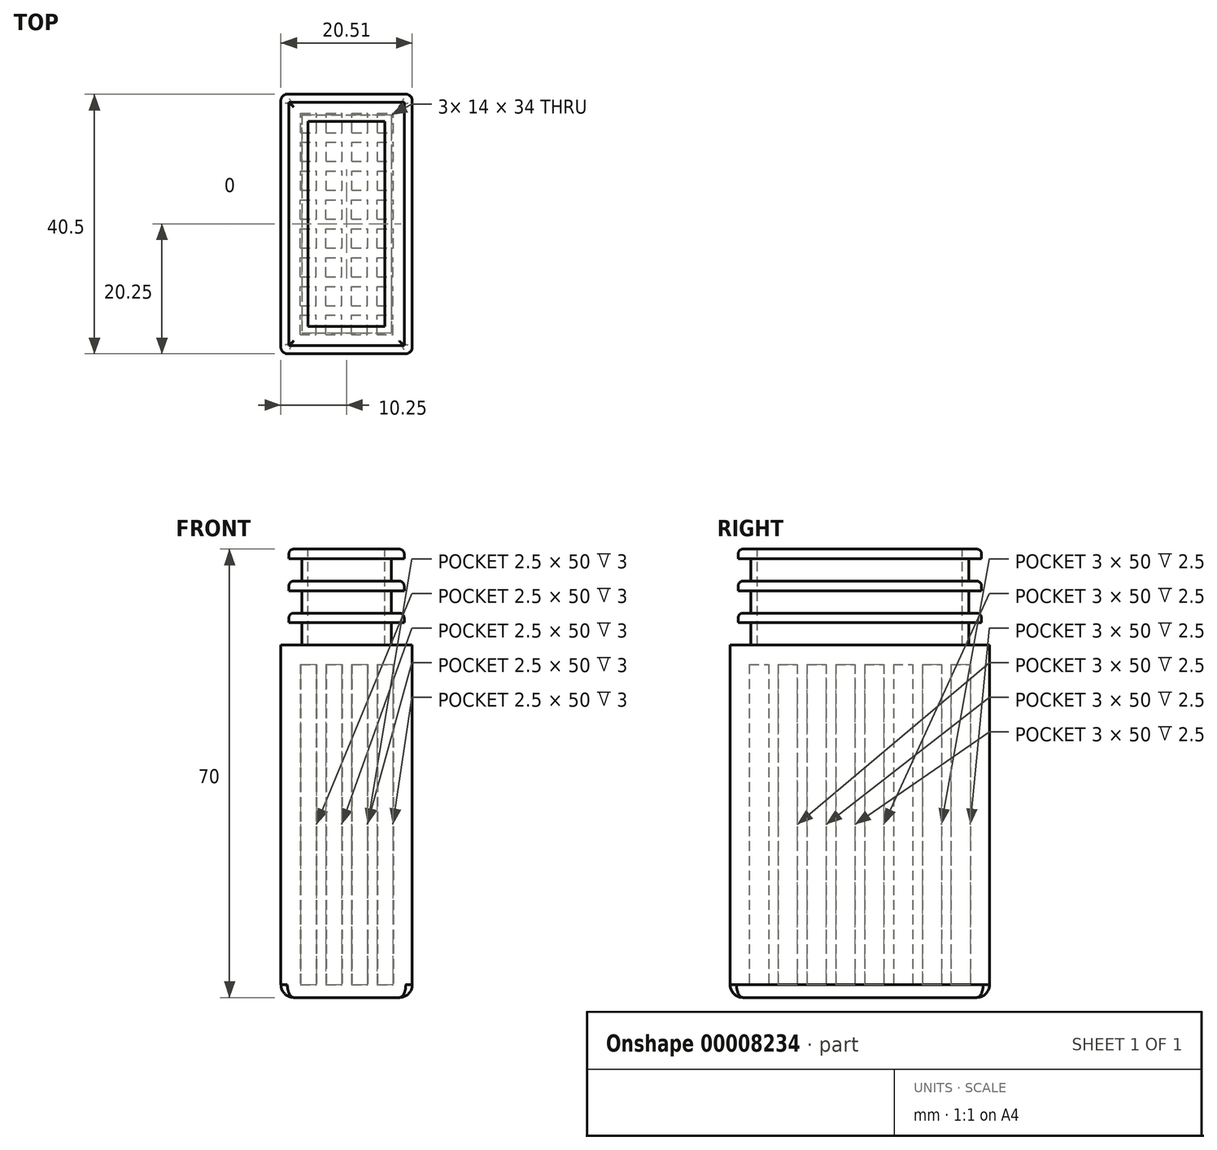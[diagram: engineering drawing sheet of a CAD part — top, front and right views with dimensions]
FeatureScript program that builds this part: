
annotation { "Feature Type Name" : "Feature", "Feature Type Description" : "" }
export const myFeature = defineFeature(function(context is Context, id is Id, definition is map)
    precondition{}
    {
        {
            var Q0;
            Q0=qCreatedBy(makeId("Top.planeOp"),FACE);
            var sketch = newSketch(context, id + "F0", { "sketchPlane" : qUnion([Q0])});
            skLineSegment(sketch, "E0.rect.bottom", {"start": v(10.25, -20.25) * mm, "end": v(-10.25, -20.25) * mm});
            skLineSegment(sketch, "E0.rect.top", {"start": v(10.25, 20.25) * mm, "end": v(-10.25, 20.25) * mm});
            skLineSegment(sketch, "E0.rect.left", {"start": v(10.25, -20.25) * mm, "end": v(10.25, 20.25) * mm});
            skLineSegment(sketch, "E0.rect.right", {"start": v(-10.25, -20.25) * mm, "end": v(-10.25, 20.25) * mm});
            skPoint(sketch, "E0.rect.middle", {"position": v(0, 0) * mm});
            skSolve(sketch);
        }
        {
            var Q0;
            Q0=makeQuery(id+"F0.imprint","IMPRINT",FACE,{"disambiguationData":[TD([[makeQuery(id+"F0.imprint","IMPRINT",EDGE,{"derivedFrom":sQuery(id+"F0.wireOp",EDGE,"E0.rect.bottom")}),-1.0]])]});
            extrude(context, id + "F1", {"entities" : qUnion([Q0]), "depth" : 53 * mm});
        }
        {
            var Q0;
            Q0=makeQuery(id+"F1.opExtrude","CAP_FACE",FACE,{"disambiguationData":[OSD([sQuery(id+"F0.wireOp",EDGE,"E0.rect.bottom"),sQuery(id+"F0.wireOp",EDGE,"E0.rect.top"),sQuery(id+"F0.wireOp",EDGE,"E0.rect.left"),sQuery(id+"F0.wireOp",EDGE,"E0.rect.right")])],"isStart":false});
            var sketch = newSketch(context, id + "F2", { "sketchPlane" : qUnion([Q0])});
            skLineSegment(sketch, "E1.bottom", {"start": v(-7, 17) * mm, "end": v(7, 17) * mm});
            skLineSegment(sketch, "E1.top", {"start": v(-7, -17) * mm, "end": v(7, -17) * mm});
            skLineSegment(sketch, "E1.left", {"start": v(-7, 17) * mm, "end": v(-7, -17) * mm});
            skLineSegment(sketch, "E1.right", {"start": v(7, 17) * mm, "end": v(7, -17) * mm});
            skSolve(sketch);
        }
        {
            var Q0;
            Q0=qSketchRegion(id+"F2",true);
            extrude(context, id + "F3", {"entities" : qUnion([Q0]), "operationType" : NewBodyOperationType.ADD, "depth" : 3.5 * mm});
        }
        {
            var Q0;
            Q0=makeQuery(id+"F3.opExtrude","CAP_FACE",FACE,{"disambiguationData":[OSD([sQuery(id+"F2.wireOp",EDGE,"E1.bottom"),sQuery(id+"F2.wireOp",EDGE,"E1.top"),sQuery(id+"F2.wireOp",EDGE,"E1.left"),sQuery(id+"F2.wireOp",EDGE,"E1.right")])],"isStart":false});
            var sketch = newSketch(context, id + "F4", { "sketchPlane" : qUnion([Q0])});
            skLineSegment(sketch, "E2.bottom", {"start": v(-9, 19) * mm, "end": v(9, 19) * mm});
            skLineSegment(sketch, "E2.top", {"start": v(-9, -19) * mm, "end": v(9, -19) * mm});
            skLineSegment(sketch, "E2.left", {"start": v(-9, 19) * mm, "end": v(-9, -19) * mm});
            skLineSegment(sketch, "E2.right", {"start": v(9, 19) * mm, "end": v(9, -19) * mm});
            skSolve(sketch);
        }
        {
            var Q0;
            Q0=qSketchRegion(id+"F4",true);
            extrude(context, id + "F5", {"entities" : qUnion([Q0]), "operationType" : NewBodyOperationType.ADD, "depth" : 1.5 * mm});
        }
        {
            var Q0;
            Q0=makeQuery(id+"F5.opExtrude","CAP_FACE",FACE,{"disambiguationData":[OSD([sQuery(id+"F4.wireOp",EDGE,"E2.bottom"),sQuery(id+"F4.wireOp",EDGE,"E2.top"),sQuery(id+"F4.wireOp",EDGE,"E2.left"),sQuery(id+"F4.wireOp",EDGE,"E2.right")])],"isStart":false});
            fillet(context, id + "F6", {"entities" : qUnion([Q0]), "radius" : 0.75 * mm, "tangentPropagation" : true, "allowEdgeOverflow" : false});
        }
        {
            var Q0;
            Q0=makeQuery(id+"F5.opExtrude","CAP_FACE",FACE,{"disambiguationData":[OSD([sQuery(id+"F4.wireOp",EDGE,"E2.bottom"),sQuery(id+"F4.wireOp",EDGE,"E2.top"),sQuery(id+"F4.wireOp",EDGE,"E2.left"),sQuery(id+"F4.wireOp",EDGE,"E2.right")])],"isStart":false});
            var sketch = newSketch(context, id + "F7", { "sketchPlane" : qUnion([Q0])});
            skLineSegment(sketch, "E3.rect.bottom", {"start": v(-7, -17) * mm, "end": v(7, -17) * mm});
            skLineSegment(sketch, "E3.rect.top", {"start": v(-7, 17) * mm, "end": v(7, 17) * mm});
            skLineSegment(sketch, "E3.rect.left", {"start": v(-7, -17) * mm, "end": v(-7, 17) * mm});
            skLineSegment(sketch, "E3.rect.right", {"start": v(7, -17) * mm, "end": v(7, 17) * mm});
            skPoint(sketch, "E3.rect.middle", {"position": v(0, 0) * mm});
            skSolve(sketch);
        }
        {
            var Q0;
            Q0=qSketchRegion(id+"F7",true);
            extrude(context, id + "F8", {"entities" : qUnion([Q0]), "operationType" : NewBodyOperationType.ADD, "depth" : 3.5 * mm});
        }
        {
            var Q0;
            Q0=makeQuery(id+"F8.opExtrude","CAP_FACE",FACE,{"disambiguationData":[OSD([sQuery(id+"F7.wireOp",EDGE,"E3.rect.bottom"),sQuery(id+"F7.wireOp",EDGE,"E3.rect.top"),sQuery(id+"F7.wireOp",EDGE,"E3.rect.left"),sQuery(id+"F7.wireOp",EDGE,"E3.rect.right")])],"isStart":false});
            var sketch = newSketch(context, id + "F9", { "sketchPlane" : qUnion([Q0])});
            skLineSegment(sketch, "E4.bottom", {"start": v(-9, 19) * mm, "end": v(9, 19) * mm});
            skLineSegment(sketch, "E4.top", {"start": v(-9, -19) * mm, "end": v(9, -19) * mm});
            skLineSegment(sketch, "E4.left", {"start": v(-9, 19) * mm, "end": v(-9, -19) * mm});
            skLineSegment(sketch, "E4.right", {"start": v(9, 19) * mm, "end": v(9, -19) * mm});
            skSolve(sketch);
        }
        {
            var Q0;
            Q0=qSketchRegion(id+"F9",true);
            extrude(context, id + "F10", {"entities" : qUnion([Q0]), "operationType" : NewBodyOperationType.ADD, "depth" : 1.5 * mm});
        }
        {
            var Q0;
            Q0=makeQuery(id+"F10.opExtrude","CAP_FACE",FACE,{"disambiguationData":[OSD([sQuery(id+"F9.wireOp",EDGE,"E4.bottom"),sQuery(id+"F9.wireOp",EDGE,"E4.top"),sQuery(id+"F9.wireOp",EDGE,"E4.left"),sQuery(id+"F9.wireOp",EDGE,"E4.right")])],"isStart":false});
            var sketch = newSketch(context, id + "F11", { "sketchPlane" : qUnion([Q0])});
            skLineSegment(sketch, "E5.bottom", {"start": v(-7, 17) * mm, "end": v(7, 17) * mm});
            skLineSegment(sketch, "E5.top", {"start": v(-7, -17) * mm, "end": v(7, -17) * mm});
            skLineSegment(sketch, "E5.left", {"start": v(-7, 17) * mm, "end": v(-7, -17) * mm});
            skLineSegment(sketch, "E5.right", {"start": v(7, 17) * mm, "end": v(7, -17) * mm});
            skSolve(sketch);
        }
        {
            var Q0;
            Q0=qSketchRegion(id+"F11",true);
            extrude(context, id + "F12", {"entities" : qUnion([Q0]), "operationType" : NewBodyOperationType.ADD, "depth" : 3.5 * mm});
        }
        {
            var Q0;
            Q0=makeQuery(id+"F12.opExtrude","CAP_FACE",FACE,{"disambiguationData":[OSD([sQuery(id+"F11.wireOp",EDGE,"E5.bottom"),sQuery(id+"F11.wireOp",EDGE,"E5.top"),sQuery(id+"F11.wireOp",EDGE,"E5.left"),sQuery(id+"F11.wireOp",EDGE,"E5.right")])],"isStart":false});
            var sketch = newSketch(context, id + "F13", { "sketchPlane" : qUnion([Q0])});
            skLineSegment(sketch, "E6.bottom", {"start": v(-9, 19) * mm, "end": v(9, 19) * mm});
            skLineSegment(sketch, "E6.top", {"start": v(-9, -19) * mm, "end": v(9, -19) * mm});
            skLineSegment(sketch, "E6.left", {"start": v(-9, 19) * mm, "end": v(-9, -19) * mm});
            skLineSegment(sketch, "E6.right", {"start": v(9, 19) * mm, "end": v(9, -19) * mm});
            skSolve(sketch);
        }
        {
            var Q0;
            Q0=makeQuery(id+"F13.imprint","IMPRINT",FACE,{"disambiguationData":[TD([[makeQuery(id+"F13.imprint","IMPRINT",EDGE,{"derivedFrom":sQuery(id+"F13.wireOp",EDGE,"E6.bottom")}),-1.0]])]});
            var Q1;
            Q1=makeQuery(id+"F13.imprint","IMPRINT",FACE,{"disambiguationData":[TD([[makeQuery(id+"F13.imprint","IMPRINT",EDGE,{"derivedFrom":makeQuery(id+"F12.opExtrude","CAP_EDGE",EDGE,{"disambiguationData":[OSD([sQuery(id+"F11.wireOp",EDGE,"E5.bottom")])],"isStart":false})}),-1.0]])]});
            extrude(context, id + "F14", {"entities" : qUnion([Q0, Q1]), "operationType" : NewBodyOperationType.ADD, "depth" : 1.5 * mm});
        }
        {
            var Q0;
            Q0=makeQuery(id+"F10.opExtrude","CAP_EDGE",EDGE,{"disambiguationData":[OSD([sQuery(id+"F9.wireOp",EDGE,"E4.bottom")])],"isStart":false});
            var Q1;
            Q1=makeQuery(id+"F10.opExtrude","CAP_EDGE",EDGE,{"disambiguationData":[OSD([sQuery(id+"F9.wireOp",EDGE,"E4.left")])],"isStart":false});
            var Q2;
            Q2=makeQuery(id+"F10.opExtrude","CAP_EDGE",EDGE,{"disambiguationData":[OSD([sQuery(id+"F9.wireOp",EDGE,"E4.right")])],"isStart":false});
            var Q3;
            Q3=makeQuery(id+"F10.opExtrude","CAP_EDGE",EDGE,{"disambiguationData":[OSD([sQuery(id+"F9.wireOp",EDGE,"E4.top")])],"isStart":false});
            fillet(context, id + "F15", {"entities" : qUnion([Q0, Q1, Q2, Q3]), "radius" : 0.75 * mm, "tangentPropagation" : true, "allowEdgeOverflow" : false});
        }
        {
            var Q0;
            Q0=makeQuery(id+"F14.opExtrude","CAP_EDGE",EDGE,{"disambiguationData":[OSD([sQuery(id+"F13.wireOp",EDGE,"E6.left")])],"isStart":false});
            var Q1;
            Q1=makeQuery(id+"F14.opExtrude","CAP_EDGE",EDGE,{"disambiguationData":[OSD([sQuery(id+"F13.wireOp",EDGE,"E6.top")])],"isStart":false});
            var Q2;
            Q2=makeQuery(id+"F14.opExtrude","CAP_EDGE",EDGE,{"disambiguationData":[OSD([sQuery(id+"F13.wireOp",EDGE,"E6.right")])],"isStart":false});
            var Q3;
            Q3=makeQuery(id+"F14.opExtrude","CAP_EDGE",EDGE,{"disambiguationData":[OSD([sQuery(id+"F13.wireOp",EDGE,"E6.bottom")])],"isStart":false});
            fillet(context, id + "F16", {"entities" : qUnion([Q0, Q1, Q2, Q3]), "radius" : 0.75 * mm, "tangentPropagation" : true, "allowEdgeOverflow" : false});
        }
        {
            var Q0;
            Q0=makeQuery(id+"F14.opExtrude","CAP_FACE",FACE,{"disambiguationData":[OSD([sQuery(id+"F13.wireOp",EDGE,"E6.bottom"),sQuery(id+"F13.wireOp",EDGE,"E6.top"),sQuery(id+"F13.wireOp",EDGE,"E6.left"),sQuery(id+"F13.wireOp",EDGE,"E6.right")])],"isStart":false});
            var sketch = newSketch(context, id + "F17", { "sketchPlane" : qUnion([Q0])});
            skLineSegment(sketch, "E7.bottom", {"start": v(-6, 16) * mm, "end": v(6, 16) * mm});
            skLineSegment(sketch, "E7.top", {"start": v(-6, -16) * mm, "end": v(6, -16) * mm});
            skLineSegment(sketch, "E7.left", {"start": v(-6, 16) * mm, "end": v(-6, -16) * mm});
            skLineSegment(sketch, "E7.right", {"start": v(6, 16) * mm, "end": v(6, -16) * mm});
            skSolve(sketch);
        }
        {
            var Q0;
            Q0=makeQuery(id+"F17.imprint","IMPRINT",FACE,{"disambiguationData":[TD([[makeQuery(id+"F17.imprint","IMPRINT",EDGE,{"derivedFrom":sQuery(id+"F17.wireOp",EDGE,"E7.bottom")}),-1.0]])]});
            var Q1;
            Q1=makeQuery(id+"F1.opExtrude","CAP_FACE",FACE,{"disambiguationData":[OSD([sQuery(id+"F0.wireOp",EDGE,"E0.rect.bottom"),sQuery(id+"F0.wireOp",EDGE,"E0.rect.top"),sQuery(id+"F0.wireOp",EDGE,"E0.rect.left"),sQuery(id+"F0.wireOp",EDGE,"E0.rect.right")])],"isStart":false});
            extrude(context, id + "F18", {"entities" : qUnion([Q0]), "operationType" : NewBodyOperationType.REMOVE, "oppositeDirection" : true, "endBoundEntity" : qUnion([Q1]), "depth" : 15 * mm});
        }
        {
            var Q0;
            Q0=makeQuery(id+"F1.opExtrude","SWEPT_EDGE",EDGE,{"disambiguationData":[OSD([sQuery(id+"F0.wireOp",EDGE,"E0.rect.bottom"),sQuery(id+"F0.wireOp",EDGE,"E0.rect.left")])]});
            var Q1;
            Q1=makeQuery(id+"F1.opExtrude","SWEPT_EDGE",EDGE,{"disambiguationData":[OSD([sQuery(id+"F0.wireOp",EDGE,"E0.rect.top"),sQuery(id+"F0.wireOp",EDGE,"E0.rect.left")])]});
            var Q2;
            Q2=makeQuery(id+"F1.opExtrude","SWEPT_EDGE",EDGE,{"disambiguationData":[OSD([sQuery(id+"F0.wireOp",EDGE,"E0.rect.top"),sQuery(id+"F0.wireOp",EDGE,"E0.rect.right")])]});
            var Q3;
            Q3=makeQuery(id+"F1.opExtrude","SWEPT_EDGE",EDGE,{"disambiguationData":[OSD([sQuery(id+"F0.wireOp",EDGE,"E0.rect.bottom"),sQuery(id+"F0.wireOp",EDGE,"E0.rect.right")])]});
            fillet(context, id + "F19", {"entities" : qUnion([Q0, Q1, Q2, Q3]), "radius" : 1 * mm, "tangentPropagation" : true, "allowEdgeOverflow" : false});
        }
        {
            var Q0;
            Q0=makeQuery(id+"F1.opExtrude","CAP_FACE",FACE,{"disambiguationData":[OSD([sQuery(id+"F0.wireOp",EDGE,"E0.rect.bottom"),sQuery(id+"F0.wireOp",EDGE,"E0.rect.top"),sQuery(id+"F0.wireOp",EDGE,"E0.rect.left"),sQuery(id+"F0.wireOp",EDGE,"E0.rect.right")])],"isStart":true});
            var sketch = newSketch(context, id + "F20", { "sketchPlane" : qUnion([Q0])});
            skLineSegment(sketch, "E8.bottom", {"start": v(-7.25, 17.25) * mm, "end": v(-4.75, 17.25) * mm});
            skLineSegment(sketch, "E8.top", {"start": v(-7.25, 14.25) * mm, "end": v(-4.75, 14.25) * mm});
            skLineSegment(sketch, "E8.left", {"start": v(-7.25, 17.25) * mm, "end": v(-7.25, 14.25) * mm});
            skLineSegment(sketch, "E8.right", {"start": v(-4.75, 17.25) * mm, "end": v(-4.75, 14.25) * mm});
            skLineSegment(sketch, "E9.1.0.0", {"start": v(-3.25, 17.25) * mm, "end": v(-0.75, 17.25) * mm});
            skLineSegment(sketch, "E9.1.0.1", {"start": v(-0.75, 17.25) * mm, "end": v(-0.75, 14.25) * mm});
            skLineSegment(sketch, "E9.1.0.2", {"start": v(-3.25, 17.25) * mm, "end": v(-3.25, 14.25) * mm});
            skLineSegment(sketch, "E9.1.0.3", {"start": v(-3.25, 14.25) * mm, "end": v(-0.75, 14.25) * mm});
            skLineSegment(sketch, "E9.2.0.0", {"start": v(0.75, 17.25) * mm, "end": v(3.25, 17.25) * mm});
            skLineSegment(sketch, "E9.2.0.1", {"start": v(3.25, 17.25) * mm, "end": v(3.25, 14.25) * mm});
            skLineSegment(sketch, "E9.2.0.2", {"start": v(0.75, 17.25) * mm, "end": v(0.75, 14.25) * mm});
            skLineSegment(sketch, "E9.2.0.3", {"start": v(0.75, 14.25) * mm, "end": v(3.25, 14.25) * mm});
            skLineSegment(sketch, "E9.3.0.0", {"start": v(4.75, 17.25) * mm, "end": v(7.25, 17.25) * mm});
            skLineSegment(sketch, "E9.3.0.1", {"start": v(7.25, 17.25) * mm, "end": v(7.25, 14.25) * mm});
            skLineSegment(sketch, "E9.3.0.2", {"start": v(4.75, 17.25) * mm, "end": v(4.75, 14.25) * mm});
            skLineSegment(sketch, "E9.3.0.3", {"start": v(4.75, 14.25) * mm, "end": v(7.25, 14.25) * mm});
            skLineSegment(sketch, "E9.direction1", {"start": v(-7.25, 17.25) * mm, "end": v(-3.25, 17.25) * mm, "construction": true});
            skLineSegment(sketch, "E10.1.0.0", {"start": v(-7.24, 12.75) * mm, "end": v(-7.24, 9.75) * mm});
            skLineSegment(sketch, "E10.1.0.1", {"start": v(-3.24, 12.75) * mm, "end": v(-3.24, 9.75) * mm});
            skLineSegment(sketch, "E10.1.0.2", {"start": v(-3.24, 9.75) * mm, "end": v(-0.74, 9.75) * mm});
            skLineSegment(sketch, "E10.1.0.3", {"start": v(4.76, 9.75) * mm, "end": v(7.26, 9.75) * mm});
            skLineSegment(sketch, "E10.1.0.4", {"start": v(-7.24, 9.75) * mm, "end": v(-4.74, 9.75) * mm});
            skLineSegment(sketch, "E10.1.0.5", {"start": v(-7.24, 12.75) * mm, "end": v(-4.74, 12.75) * mm});
            skLineSegment(sketch, "E10.1.0.6", {"start": v(4.76, 12.75) * mm, "end": v(4.76, 9.75) * mm});
            skLineSegment(sketch, "E10.1.0.7", {"start": v(-0.74, 12.75) * mm, "end": v(-0.74, 9.75) * mm});
            skLineSegment(sketch, "E10.1.0.8", {"start": v(-7.24, 12.75) * mm, "end": v(-3.24, 12.75) * mm, "construction": true});
            skLineSegment(sketch, "E10.1.0.9", {"start": v(0.76, 9.75) * mm, "end": v(3.26, 9.75) * mm});
            skLineSegment(sketch, "E10.1.0.10", {"start": v(4.76, 12.75) * mm, "end": v(7.26, 12.75) * mm});
            skLineSegment(sketch, "E10.1.0.11", {"start": v(0.76, 12.75) * mm, "end": v(3.26, 12.75) * mm});
            skLineSegment(sketch, "E10.1.0.12", {"start": v(3.26, 12.75) * mm, "end": v(3.26, 9.75) * mm});
            skLineSegment(sketch, "E10.1.0.13", {"start": v(7.26, 12.75) * mm, "end": v(7.26, 9.75) * mm});
            skLineSegment(sketch, "E10.1.0.14", {"start": v(0.76, 12.75) * mm, "end": v(0.76, 9.75) * mm});
            skLineSegment(sketch, "E10.1.0.15", {"start": v(-3.24, 12.75) * mm, "end": v(-0.74, 12.75) * mm});
            skLineSegment(sketch, "E10.1.0.16", {"start": v(-4.74, 12.75) * mm, "end": v(-4.74, 9.75) * mm});
            skLineSegment(sketch, "E10.2.0.0", {"start": v(-7.22, 8.25) * mm, "end": v(-7.22, 5.25) * mm});
            skLineSegment(sketch, "E10.2.0.1", {"start": v(-3.22, 8.25) * mm, "end": v(-3.22, 5.25) * mm});
            skLineSegment(sketch, "E10.2.0.2", {"start": v(-3.22, 5.25) * mm, "end": v(-0.72, 5.25) * mm});
            skLineSegment(sketch, "E10.2.0.3", {"start": v(4.78, 5.25) * mm, "end": v(7.28, 5.25) * mm});
            skLineSegment(sketch, "E10.2.0.4", {"start": v(-7.22, 5.25) * mm, "end": v(-4.72, 5.25) * mm});
            skLineSegment(sketch, "E10.2.0.5", {"start": v(-7.22, 8.25) * mm, "end": v(-4.72, 8.25) * mm});
            skLineSegment(sketch, "E10.2.0.6", {"start": v(4.78, 8.25) * mm, "end": v(4.78, 5.25) * mm});
            skLineSegment(sketch, "E10.2.0.7", {"start": v(-0.72, 8.25) * mm, "end": v(-0.72, 5.25) * mm});
            skLineSegment(sketch, "E10.2.0.8", {"start": v(-7.22, 8.25) * mm, "end": v(-3.22, 8.25) * mm, "construction": true});
            skLineSegment(sketch, "E10.2.0.9", {"start": v(0.78, 5.25) * mm, "end": v(3.28, 5.25) * mm});
            skLineSegment(sketch, "E10.2.0.10", {"start": v(4.78, 8.25) * mm, "end": v(7.28, 8.25) * mm});
            skLineSegment(sketch, "E10.2.0.11", {"start": v(0.78, 8.25) * mm, "end": v(3.28, 8.25) * mm});
            skLineSegment(sketch, "E10.2.0.12", {"start": v(3.28, 8.25) * mm, "end": v(3.28, 5.25) * mm});
            skLineSegment(sketch, "E10.2.0.13", {"start": v(7.28, 8.25) * mm, "end": v(7.28, 5.25) * mm});
            skLineSegment(sketch, "E10.2.0.14", {"start": v(0.78, 8.25) * mm, "end": v(0.78, 5.25) * mm});
            skLineSegment(sketch, "E10.2.0.15", {"start": v(-3.22, 8.25) * mm, "end": v(-0.72, 8.25) * mm});
            skLineSegment(sketch, "E10.2.0.16", {"start": v(-4.72, 8.25) * mm, "end": v(-4.72, 5.25) * mm});
            skLineSegment(sketch, "E10.3.0.0", {"start": v(-7.21, 3.75) * mm, "end": v(-7.21, 0.75) * mm});
            skLineSegment(sketch, "E10.3.0.1", {"start": v(-3.21, 3.75) * mm, "end": v(-3.21, 0.75) * mm});
            skLineSegment(sketch, "E10.3.0.2", {"start": v(-3.21, 0.75) * mm, "end": v(-0.71, 0.75) * mm});
            skLineSegment(sketch, "E10.3.0.3", {"start": v(4.79, 0.75) * mm, "end": v(7.29, 0.75) * mm});
            skLineSegment(sketch, "E10.3.0.4", {"start": v(-7.21, 0.75) * mm, "end": v(-4.71, 0.75) * mm});
            skLineSegment(sketch, "E10.3.0.5", {"start": v(-7.21, 3.75) * mm, "end": v(-4.71, 3.75) * mm});
            skLineSegment(sketch, "E10.3.0.6", {"start": v(4.79, 3.75) * mm, "end": v(4.79, 0.75) * mm});
            skLineSegment(sketch, "E10.3.0.7", {"start": v(-0.71, 3.75) * mm, "end": v(-0.71, 0.75) * mm});
            skLineSegment(sketch, "E10.3.0.8", {"start": v(-7.21, 3.75) * mm, "end": v(-3.21, 3.75) * mm, "construction": true});
            skLineSegment(sketch, "E10.3.0.9", {"start": v(0.79, 0.75) * mm, "end": v(3.29, 0.75) * mm});
            skLineSegment(sketch, "E10.3.0.10", {"start": v(4.79, 3.75) * mm, "end": v(7.29, 3.75) * mm});
            skLineSegment(sketch, "E10.3.0.11", {"start": v(0.79, 3.75) * mm, "end": v(3.29, 3.75) * mm});
            skLineSegment(sketch, "E10.3.0.12", {"start": v(3.29, 3.75) * mm, "end": v(3.29, 0.75) * mm});
            skLineSegment(sketch, "E10.3.0.13", {"start": v(7.29, 3.75) * mm, "end": v(7.29, 0.75) * mm});
            skLineSegment(sketch, "E10.3.0.14", {"start": v(0.79, 3.75) * mm, "end": v(0.79, 0.75) * mm});
            skLineSegment(sketch, "E10.3.0.15", {"start": v(-3.21, 3.75) * mm, "end": v(-0.71, 3.75) * mm});
            skLineSegment(sketch, "E10.3.0.16", {"start": v(-4.71, 3.75) * mm, "end": v(-4.71, 0.75) * mm});
            skLineSegment(sketch, "E10.4.0.0", {"start": v(-7.2, -0.75) * mm, "end": v(-7.2, -3.75) * mm});
            skLineSegment(sketch, "E10.4.0.1", {"start": v(-3.2, -0.75) * mm, "end": v(-3.2, -3.75) * mm});
            skLineSegment(sketch, "E10.4.0.2", {"start": v(-3.2, -3.75) * mm, "end": v(-0.7, -3.75) * mm});
            skLineSegment(sketch, "E10.4.0.3", {"start": v(4.8, -3.75) * mm, "end": v(7.3, -3.75) * mm});
            skLineSegment(sketch, "E10.4.0.4", {"start": v(-7.2, -3.75) * mm, "end": v(-4.7, -3.75) * mm});
            skLineSegment(sketch, "E10.4.0.5", {"start": v(-7.2, -0.75) * mm, "end": v(-4.7, -0.75) * mm});
            skLineSegment(sketch, "E10.4.0.6", {"start": v(4.8, -0.75) * mm, "end": v(4.8, -3.75) * mm});
            skLineSegment(sketch, "E10.4.0.7", {"start": v(-0.7, -0.75) * mm, "end": v(-0.7, -3.75) * mm});
            skLineSegment(sketch, "E10.4.0.8", {"start": v(-7.2, -0.75) * mm, "end": v(-3.2, -0.75) * mm, "construction": true});
            skLineSegment(sketch, "E10.4.0.9", {"start": v(0.8, -3.75) * mm, "end": v(3.3, -3.75) * mm});
            skLineSegment(sketch, "E10.4.0.10", {"start": v(4.8, -0.75) * mm, "end": v(7.3, -0.75) * mm});
            skLineSegment(sketch, "E10.4.0.11", {"start": v(0.8, -0.75) * mm, "end": v(3.3, -0.75) * mm});
            skLineSegment(sketch, "E10.4.0.12", {"start": v(3.3, -0.75) * mm, "end": v(3.3, -3.75) * mm});
            skLineSegment(sketch, "E10.4.0.13", {"start": v(7.3, -0.75) * mm, "end": v(7.3, -3.75) * mm});
            skLineSegment(sketch, "E10.4.0.14", {"start": v(0.8, -0.75) * mm, "end": v(0.8, -3.75) * mm});
            skLineSegment(sketch, "E10.4.0.15", {"start": v(-3.2, -0.75) * mm, "end": v(-0.7, -0.75) * mm});
            skLineSegment(sketch, "E10.4.0.16", {"start": v(-4.7, -0.75) * mm, "end": v(-4.7, -3.75) * mm});
            skLineSegment(sketch, "E10.5.0.0", {"start": v(-7.18, -5.25) * mm, "end": v(-7.18, -8.25) * mm});
            skLineSegment(sketch, "E10.5.0.1", {"start": v(-3.18, -5.25) * mm, "end": v(-3.18, -8.25) * mm});
            skLineSegment(sketch, "E10.5.0.2", {"start": v(-3.18, -8.25) * mm, "end": v(-0.68, -8.25) * mm});
            skLineSegment(sketch, "E10.5.0.3", {"start": v(4.82, -8.25) * mm, "end": v(7.32, -8.25) * mm});
            skLineSegment(sketch, "E10.5.0.4", {"start": v(-7.18, -8.25) * mm, "end": v(-4.68, -8.25) * mm});
            skLineSegment(sketch, "E10.5.0.5", {"start": v(-7.18, -5.25) * mm, "end": v(-4.68, -5.25) * mm});
            skLineSegment(sketch, "E10.5.0.6", {"start": v(4.82, -5.25) * mm, "end": v(4.82, -8.25) * mm});
            skLineSegment(sketch, "E10.5.0.7", {"start": v(-0.68, -5.25) * mm, "end": v(-0.68, -8.25) * mm});
            skLineSegment(sketch, "E10.5.0.8", {"start": v(-7.18, -5.25) * mm, "end": v(-3.18, -5.25) * mm, "construction": true});
            skLineSegment(sketch, "E10.5.0.9", {"start": v(0.82, -8.25) * mm, "end": v(3.32, -8.25) * mm});
            skLineSegment(sketch, "E10.5.0.10", {"start": v(4.82, -5.25) * mm, "end": v(7.32, -5.25) * mm});
            skLineSegment(sketch, "E10.5.0.11", {"start": v(0.82, -5.25) * mm, "end": v(3.32, -5.25) * mm});
            skLineSegment(sketch, "E10.5.0.12", {"start": v(3.32, -5.25) * mm, "end": v(3.32, -8.25) * mm});
            skLineSegment(sketch, "E10.5.0.13", {"start": v(7.32, -5.25) * mm, "end": v(7.32, -8.25) * mm});
            skLineSegment(sketch, "E10.5.0.14", {"start": v(0.82, -5.25) * mm, "end": v(0.82, -8.25) * mm});
            skLineSegment(sketch, "E10.5.0.15", {"start": v(-3.18, -5.25) * mm, "end": v(-0.68, -5.25) * mm});
            skLineSegment(sketch, "E10.5.0.16", {"start": v(-4.68, -5.25) * mm, "end": v(-4.68, -8.25) * mm});
            skLineSegment(sketch, "E10.6.0.0", {"start": v(-7.17, -9.75) * mm, "end": v(-7.17, -12.75) * mm});
            skLineSegment(sketch, "E10.6.0.1", {"start": v(-3.17, -9.75) * mm, "end": v(-3.17, -12.75) * mm});
            skLineSegment(sketch, "E10.6.0.2", {"start": v(-3.17, -12.75) * mm, "end": v(-0.67, -12.75) * mm});
            skLineSegment(sketch, "E10.6.0.3", {"start": v(4.83, -12.75) * mm, "end": v(7.33, -12.75) * mm});
            skLineSegment(sketch, "E10.6.0.4", {"start": v(-7.17, -12.75) * mm, "end": v(-4.67, -12.75) * mm});
            skLineSegment(sketch, "E10.6.0.5", {"start": v(-7.17, -9.75) * mm, "end": v(-4.67, -9.75) * mm});
            skLineSegment(sketch, "E10.6.0.6", {"start": v(4.83, -9.75) * mm, "end": v(4.83, -12.75) * mm});
            skLineSegment(sketch, "E10.6.0.7", {"start": v(-0.67, -9.75) * mm, "end": v(-0.67, -12.75) * mm});
            skLineSegment(sketch, "E10.6.0.8", {"start": v(-7.17, -9.75) * mm, "end": v(-3.17, -9.75) * mm, "construction": true});
            skLineSegment(sketch, "E10.6.0.9", {"start": v(0.83, -12.75) * mm, "end": v(3.33, -12.75) * mm});
            skLineSegment(sketch, "E10.6.0.10", {"start": v(4.83, -9.75) * mm, "end": v(7.33, -9.75) * mm});
            skLineSegment(sketch, "E10.6.0.11", {"start": v(0.83, -9.75) * mm, "end": v(3.33, -9.75) * mm});
            skLineSegment(sketch, "E10.6.0.12", {"start": v(3.33, -9.75) * mm, "end": v(3.33, -12.75) * mm});
            skLineSegment(sketch, "E10.6.0.13", {"start": v(7.33, -9.75) * mm, "end": v(7.33, -12.75) * mm});
            skLineSegment(sketch, "E10.6.0.14", {"start": v(0.83, -9.75) * mm, "end": v(0.83, -12.75) * mm});
            skLineSegment(sketch, "E10.6.0.15", {"start": v(-3.17, -9.75) * mm, "end": v(-0.67, -9.75) * mm});
            skLineSegment(sketch, "E10.6.0.16", {"start": v(-4.67, -9.75) * mm, "end": v(-4.67, -12.75) * mm});
            skLineSegment(sketch, "E10.7.0.0", {"start": v(-7.16, -14.25) * mm, "end": v(-7.16, -17.25) * mm});
            skLineSegment(sketch, "E10.7.0.1", {"start": v(-3.16, -14.25) * mm, "end": v(-3.16, -17.25) * mm});
            skLineSegment(sketch, "E10.7.0.2", {"start": v(-3.16, -17.25) * mm, "end": v(-0.66, -17.25) * mm});
            skLineSegment(sketch, "E10.7.0.3", {"start": v(4.84, -17.25) * mm, "end": v(7.34, -17.25) * mm});
            skLineSegment(sketch, "E10.7.0.4", {"start": v(-7.16, -17.25) * mm, "end": v(-4.66, -17.25) * mm});
            skLineSegment(sketch, "E10.7.0.5", {"start": v(-7.16, -14.25) * mm, "end": v(-4.66, -14.25) * mm});
            skLineSegment(sketch, "E10.7.0.6", {"start": v(4.84, -14.25) * mm, "end": v(4.84, -17.25) * mm});
            skLineSegment(sketch, "E10.7.0.7", {"start": v(-0.66, -14.25) * mm, "end": v(-0.66, -17.25) * mm});
            skLineSegment(sketch, "E10.7.0.8", {"start": v(-7.16, -14.25) * mm, "end": v(-3.16, -14.25) * mm, "construction": true});
            skLineSegment(sketch, "E10.7.0.9", {"start": v(0.84, -17.25) * mm, "end": v(3.34, -17.25) * mm});
            skLineSegment(sketch, "E10.7.0.10", {"start": v(4.84, -14.25) * mm, "end": v(7.34, -14.25) * mm});
            skLineSegment(sketch, "E10.7.0.11", {"start": v(0.84, -14.25) * mm, "end": v(3.34, -14.25) * mm});
            skLineSegment(sketch, "E10.7.0.12", {"start": v(3.34, -14.25) * mm, "end": v(3.34, -17.25) * mm});
            skLineSegment(sketch, "E10.7.0.13", {"start": v(7.34, -14.25) * mm, "end": v(7.34, -17.25) * mm});
            skLineSegment(sketch, "E10.7.0.14", {"start": v(0.84, -14.25) * mm, "end": v(0.84, -17.25) * mm});
            skLineSegment(sketch, "E10.7.0.15", {"start": v(-3.16, -14.25) * mm, "end": v(-0.66, -14.25) * mm});
            skLineSegment(sketch, "E10.7.0.16", {"start": v(-4.66, -14.25) * mm, "end": v(-4.66, -17.25) * mm});
            skLineSegment(sketch, "E10.direction1", {"start": v(-7.25, 14.25) * mm, "end": v(-7.24, 9.75) * mm, "construction": true});
            skSolve(sketch);
        }
        {
            var Q0;
            Q0=makeQuery(id+"F20.imprint","IMPRINT",FACE,{"disambiguationData":[TD([[makeQuery(id+"F20.imprint","IMPRINT",EDGE,{"derivedFrom":sQuery(id+"F20.wireOp",EDGE,"E8.bottom")}),-1.0]])]});
            var Q1;
            Q1=makeQuery(id+"F20.imprint","IMPRINT",FACE,{"disambiguationData":[TD([[makeQuery(id+"F20.imprint","IMPRINT",EDGE,{"derivedFrom":sQuery(id+"F20.wireOp",EDGE,"E9.1.0.0")}),-1.0]])]});
            var Q2;
            Q2=makeQuery(id+"F20.imprint","IMPRINT",FACE,{"disambiguationData":[TD([[makeQuery(id+"F20.imprint","IMPRINT",EDGE,{"derivedFrom":sQuery(id+"F20.wireOp",EDGE,"E9.2.0.0")}),-1.0]])]});
            var Q3;
            Q3=makeQuery(id+"F20.imprint","IMPRINT",FACE,{"disambiguationData":[TD([[makeQuery(id+"F20.imprint","IMPRINT",EDGE,{"derivedFrom":sQuery(id+"F20.wireOp",EDGE,"E9.3.0.0")}),-1.0]])]});
            var Q4;
            Q4=makeQuery(id+"F20.imprint","IMPRINT",FACE,{"disambiguationData":[TD([[makeQuery(id+"F20.imprint","IMPRINT",EDGE,{"derivedFrom":sQuery(id+"F20.wireOp",EDGE,"E10.1.0.0")}),1.0]])]});
            var Q5;
            Q5=makeQuery(id+"F20.imprint","IMPRINT",FACE,{"disambiguationData":[TD([[makeQuery(id+"F20.imprint","IMPRINT",EDGE,{"derivedFrom":sQuery(id+"F20.wireOp",EDGE,"E10.1.0.1")}),1.0]])]});
            var Q6;
            Q6=makeQuery(id+"F20.imprint","IMPRINT",FACE,{"disambiguationData":[TD([[makeQuery(id+"F20.imprint","IMPRINT",EDGE,{"derivedFrom":sQuery(id+"F20.wireOp",EDGE,"E10.1.0.3")}),1.0]])]});
            var Q7;
            Q7=makeQuery(id+"F20.imprint","IMPRINT",FACE,{"disambiguationData":[TD([[makeQuery(id+"F20.imprint","IMPRINT",EDGE,{"derivedFrom":sQuery(id+"F20.wireOp",EDGE,"E10.1.0.9")}),1.0]])]});
            var Q8;
            Q8=makeQuery(id+"F20.imprint","IMPRINT",FACE,{"disambiguationData":[TD([[makeQuery(id+"F20.imprint","IMPRINT",EDGE,{"derivedFrom":sQuery(id+"F20.wireOp",EDGE,"E10.2.0.0")}),1.0]])]});
            var Q9;
            Q9=makeQuery(id+"F20.imprint","IMPRINT",FACE,{"disambiguationData":[TD([[makeQuery(id+"F20.imprint","IMPRINT",EDGE,{"derivedFrom":sQuery(id+"F20.wireOp",EDGE,"E10.2.0.1")}),1.0]])]});
            var Q10;
            Q10=makeQuery(id+"F20.imprint","IMPRINT",FACE,{"disambiguationData":[TD([[makeQuery(id+"F20.imprint","IMPRINT",EDGE,{"derivedFrom":sQuery(id+"F20.wireOp",EDGE,"E10.2.0.3")}),1.0]])]});
            var Q11;
            Q11=makeQuery(id+"F20.imprint","IMPRINT",FACE,{"disambiguationData":[TD([[makeQuery(id+"F20.imprint","IMPRINT",EDGE,{"derivedFrom":sQuery(id+"F20.wireOp",EDGE,"E10.2.0.9")}),1.0]])]});
            var Q12;
            Q12=makeQuery(id+"F20.imprint","IMPRINT",FACE,{"disambiguationData":[TD([[makeQuery(id+"F20.imprint","IMPRINT",EDGE,{"derivedFrom":sQuery(id+"F20.wireOp",EDGE,"E10.3.0.0")}),1.0]])]});
            var Q13;
            Q13=makeQuery(id+"F20.imprint","IMPRINT",FACE,{"disambiguationData":[TD([[makeQuery(id+"F20.imprint","IMPRINT",EDGE,{"derivedFrom":sQuery(id+"F20.wireOp",EDGE,"E10.3.0.1")}),1.0]])]});
            var Q14;
            Q14=makeQuery(id+"F20.imprint","IMPRINT",FACE,{"disambiguationData":[TD([[makeQuery(id+"F20.imprint","IMPRINT",EDGE,{"derivedFrom":sQuery(id+"F20.wireOp",EDGE,"E10.3.0.3")}),1.0]])]});
            var Q15;
            Q15=makeQuery(id+"F20.imprint","IMPRINT",FACE,{"disambiguationData":[TD([[makeQuery(id+"F20.imprint","IMPRINT",EDGE,{"derivedFrom":sQuery(id+"F20.wireOp",EDGE,"E10.3.0.9")}),1.0]])]});
            var Q16;
            Q16=makeQuery(id+"F20.imprint","IMPRINT",FACE,{"disambiguationData":[TD([[makeQuery(id+"F20.imprint","IMPRINT",EDGE,{"derivedFrom":sQuery(id+"F20.wireOp",EDGE,"E10.4.0.0")}),1.0]])]});
            var Q17;
            Q17=makeQuery(id+"F20.imprint","IMPRINT",FACE,{"disambiguationData":[TD([[makeQuery(id+"F20.imprint","IMPRINT",EDGE,{"derivedFrom":sQuery(id+"F20.wireOp",EDGE,"E10.4.0.1")}),1.0]])]});
            var Q18;
            Q18=makeQuery(id+"F20.imprint","IMPRINT",FACE,{"disambiguationData":[TD([[makeQuery(id+"F20.imprint","IMPRINT",EDGE,{"derivedFrom":sQuery(id+"F20.wireOp",EDGE,"E10.4.0.3")}),1.0]])]});
            var Q19;
            Q19=makeQuery(id+"F20.imprint","IMPRINT",FACE,{"disambiguationData":[TD([[makeQuery(id+"F20.imprint","IMPRINT",EDGE,{"derivedFrom":sQuery(id+"F20.wireOp",EDGE,"E10.4.0.9")}),1.0]])]});
            var Q20;
            Q20=makeQuery(id+"F20.imprint","IMPRINT",FACE,{"disambiguationData":[TD([[makeQuery(id+"F20.imprint","IMPRINT",EDGE,{"derivedFrom":sQuery(id+"F20.wireOp",EDGE,"E10.5.0.0")}),1.0]])]});
            var Q21;
            Q21=makeQuery(id+"F20.imprint","IMPRINT",FACE,{"disambiguationData":[TD([[makeQuery(id+"F20.imprint","IMPRINT",EDGE,{"derivedFrom":sQuery(id+"F20.wireOp",EDGE,"E10.5.0.1")}),1.0]])]});
            var Q22;
            Q22=makeQuery(id+"F20.imprint","IMPRINT",FACE,{"disambiguationData":[TD([[makeQuery(id+"F20.imprint","IMPRINT",EDGE,{"derivedFrom":sQuery(id+"F20.wireOp",EDGE,"E10.5.0.3")}),1.0]])]});
            var Q23;
            Q23=makeQuery(id+"F20.imprint","IMPRINT",FACE,{"disambiguationData":[TD([[makeQuery(id+"F20.imprint","IMPRINT",EDGE,{"derivedFrom":sQuery(id+"F20.wireOp",EDGE,"E10.5.0.9")}),1.0]])]});
            var Q24;
            Q24=makeQuery(id+"F20.imprint","IMPRINT",FACE,{"disambiguationData":[TD([[makeQuery(id+"F20.imprint","IMPRINT",EDGE,{"derivedFrom":sQuery(id+"F20.wireOp",EDGE,"E10.6.0.0")}),1.0]])]});
            var Q25;
            Q25=makeQuery(id+"F20.imprint","IMPRINT",FACE,{"disambiguationData":[TD([[makeQuery(id+"F20.imprint","IMPRINT",EDGE,{"derivedFrom":sQuery(id+"F20.wireOp",EDGE,"E10.6.0.1")}),1.0]])]});
            var Q26;
            Q26=makeQuery(id+"F20.imprint","IMPRINT",FACE,{"disambiguationData":[TD([[makeQuery(id+"F20.imprint","IMPRINT",EDGE,{"derivedFrom":sQuery(id+"F20.wireOp",EDGE,"E10.6.0.3")}),1.0]])]});
            var Q27;
            Q27=makeQuery(id+"F20.imprint","IMPRINT",FACE,{"disambiguationData":[TD([[makeQuery(id+"F20.imprint","IMPRINT",EDGE,{"derivedFrom":sQuery(id+"F20.wireOp",EDGE,"E10.6.0.9")}),1.0]])]});
            var Q28;
            Q28=makeQuery(id+"F20.imprint","IMPRINT",FACE,{"disambiguationData":[TD([[makeQuery(id+"F20.imprint","IMPRINT",EDGE,{"derivedFrom":sQuery(id+"F20.wireOp",EDGE,"E10.7.0.0")}),1.0]])]});
            var Q29;
            Q29=makeQuery(id+"F20.imprint","IMPRINT",FACE,{"disambiguationData":[TD([[makeQuery(id+"F20.imprint","IMPRINT",EDGE,{"derivedFrom":sQuery(id+"F20.wireOp",EDGE,"E10.7.0.1")}),1.0]])]});
            var Q30;
            Q30=makeQuery(id+"F20.imprint","IMPRINT",FACE,{"disambiguationData":[TD([[makeQuery(id+"F20.imprint","IMPRINT",EDGE,{"derivedFrom":sQuery(id+"F20.wireOp",EDGE,"E10.7.0.3")}),1.0]])]});
            var Q31;
            Q31=makeQuery(id+"F20.imprint","IMPRINT",FACE,{"disambiguationData":[TD([[makeQuery(id+"F20.imprint","IMPRINT",EDGE,{"derivedFrom":sQuery(id+"F20.wireOp",EDGE,"E10.7.0.9")}),1.0]])]});
            extrude(context, id + "F21", {"entities" : qUnion([Q0, Q1, Q2, Q3, Q4, Q5, Q6, Q7, Q8, Q9, Q10, Q11, Q12, Q13, Q14, Q15, Q16, Q17, Q18, Q19, Q20, Q21, Q22, Q23, Q24, Q25, Q26, Q27, Q28, Q29, Q30, Q31]), "operationType" : NewBodyOperationType.REMOVE, "oppositeDirection" : true, "depth" : 50 * mm});
        }
        {
            var Q0;
            Q0=makeQuery(id+"F1.opExtrude","CAP_FACE",FACE,{"disambiguationData":[OSD([sQuery(id+"F0.wireOp",EDGE,"E0.rect.bottom"),sQuery(id+"F0.wireOp",EDGE,"E0.rect.top"),sQuery(id+"F0.wireOp",EDGE,"E0.rect.left"),sQuery(id+"F0.wireOp",EDGE,"E0.rect.right")])],"isStart":true});
            var sketch = newSketch(context, id + "F22", { "sketchPlane" : qUnion([Q0])});
            skLineSegment(sketch, "E11.bottom", {"start": v(-10.24, 20.25) * mm, "end": v(10.26, 20.25) * mm});
            skLineSegment(sketch, "E11.top", {"start": v(-10.24, -20.25) * mm, "end": v(10.26, -20.25) * mm});
            skLineSegment(sketch, "E11.left", {"start": v(-10.24, 20.25) * mm, "end": v(-10.24, -20.25) * mm});
            skLineSegment(sketch, "E11.right", {"start": v(10.26, 20.25) * mm, "end": v(10.26, -20.25) * mm});
            skSolve(sketch);
        }
        {
            var Q0;
            Q0=qSketchRegion(id+"F22",true);
            extrude(context, id + "F23", {"entities" : qUnion([Q0]), "operationType" : NewBodyOperationType.ADD, "depth" : 2 * mm});
        }
        {
            var Q0;
            Q0=makeQuery(id+"F23.opExtrude","CAP_EDGE",EDGE,{"disambiguationData":[OSD([sQuery(id+"F22.wireOp",EDGE,"E11.left")])],"isStart":false});
            var Q1;
            Q1=makeQuery(id+"F23.opExtrude","CAP_EDGE",EDGE,{"disambiguationData":[OSD([sQuery(id+"F22.wireOp",EDGE,"E11.bottom")])],"isStart":false});
            var Q2;
            Q2=makeQuery(id+"F23.opExtrude","CAP_EDGE",EDGE,{"disambiguationData":[OSD([sQuery(id+"F22.wireOp",EDGE,"E11.right")])],"isStart":false});
            var Q3;
            Q3=makeQuery(id+"F23.opExtrude","CAP_EDGE",EDGE,{"disambiguationData":[OSD([sQuery(id+"F22.wireOp",EDGE,"E11.top")])],"isStart":false});
            fillet(context, id + "F24", {"entities" : qUnion([Q0, Q1, Q2, Q3]), "radius" : 2 * mm, "tangentPropagation" : true, "allowEdgeOverflow" : false});
        }
        {
            var Q0;
            Q0=makeQuery(id+"F24.opFillet","BLEND_EDGE",EDGE,{"blendedFrom":[makeQuery(id+"F23.opExtrude","CAP_EDGE",EDGE,{"disambiguationData":[OSD([sQuery(id+"F22.wireOp",EDGE,"E11.bottom")])],"isStart":false}),makeQuery(id+"F23.opExtrude","CAP_EDGE",EDGE,{"disambiguationData":[OSD([sQuery(id+"F22.wireOp",EDGE,"E11.left")])],"isStart":false})],"blendedInto":[]});
            var Q1;
            Q1=makeQuery(id+"F24.opFillet","BLEND_EDGE",EDGE,{"blendedFrom":[makeQuery(id+"F23.opExtrude","CAP_EDGE",EDGE,{"disambiguationData":[OSD([sQuery(id+"F22.wireOp",EDGE,"E11.top")])],"isStart":false}),makeQuery(id+"F23.opExtrude","CAP_EDGE",EDGE,{"disambiguationData":[OSD([sQuery(id+"F22.wireOp",EDGE,"E11.left")])],"isStart":false})],"blendedInto":[]});
            var Q2;
            Q2=makeQuery(id+"F24.opFillet","BLEND_EDGE",EDGE,{"blendedFrom":[makeQuery(id+"F23.opExtrude","CAP_EDGE",EDGE,{"disambiguationData":[OSD([sQuery(id+"F22.wireOp",EDGE,"E11.bottom")])],"isStart":false}),makeQuery(id+"F23.opExtrude","CAP_EDGE",EDGE,{"disambiguationData":[OSD([sQuery(id+"F22.wireOp",EDGE,"E11.right")])],"isStart":false})],"blendedInto":[]});
            var Q3;
            Q3=makeQuery(id+"F24.opFillet","BLEND_EDGE",EDGE,{"blendedFrom":[makeQuery(id+"F23.opExtrude","CAP_EDGE",EDGE,{"disambiguationData":[OSD([sQuery(id+"F22.wireOp",EDGE,"E11.top")])],"isStart":false}),makeQuery(id+"F23.opExtrude","CAP_EDGE",EDGE,{"disambiguationData":[OSD([sQuery(id+"F22.wireOp",EDGE,"E11.right")])],"isStart":false})],"blendedInto":[]});
            fillet(context, id + "F25", {"entities" : qUnion([Q0, Q1, Q2, Q3]), "radius" : 1 * mm, "tangentPropagation" : true, "allowEdgeOverflow" : false});
        }
    });
